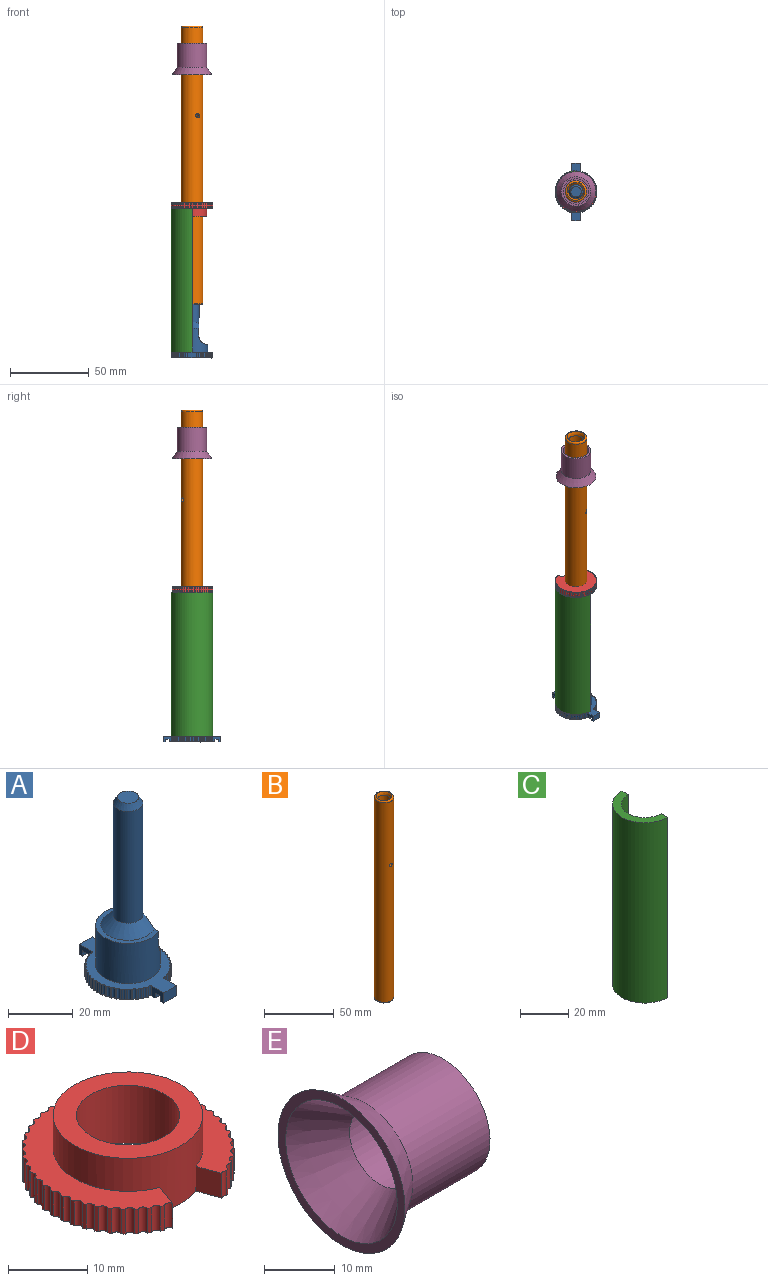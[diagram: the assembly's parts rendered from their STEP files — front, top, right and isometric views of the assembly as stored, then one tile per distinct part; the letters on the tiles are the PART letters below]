
ASSEMBLY  parts=5 mates=4
PART A: 110 faces, bbox 26.7x36.8x67.3 mm
  f0: plane 29.21x26.67mm, normal (0,0,-1), area 559.8mm2, adj f2,f3,f5,f6,f7,f8,f9,f10
  f1: plane 5.51x1.27mm, normal (0,0,-1), area 7mm2, adj f2,f99,f100,f106
  f2: plane 5.37x3.81mm, normal (1,0,0), area 15.6mm2, adj f0,f1,f49,f86,f100,f106,f107,f108
  f3: plane 5.37x3.81mm, normal (1,0,0), area 15.6mm2, adj f0,f4,f49,f54,f102,f103,f104,f105
  f4: plane 5.51x1.27mm, normal (0,0,-1), area 7mm2, adj f3,f101,f102,f104
  f5: cylinder r=13.33mm len=3.81mm, axis (0,0,-1), area 2mm2, adj f0,f49,f64,f96
  f6: cylinder r=13.33mm len=3.81mm, axis (0,0,-1), area 2mm2, adj f0,f49,f95,f96
  f7: cylinder r=13.33mm len=3.81mm, axis (0,0,-1), area 2mm2, adj f0,f49,f94,f95
  f8: cylinder r=13.33mm len=3.81mm, axis (0,0,-1), area 2mm2, adj f0,f49,f93,f94
  f9: cylinder r=13.33mm len=3.81mm, axis (0,0,-1), area 2mm2, adj f0,f49,f91,f92
  f10: cylinder r=13.33mm len=3.81mm, axis (0,0,-1), area 2mm2, adj f0,f49,f90,f91
  f11: cylinder r=13.33mm len=3.81mm, axis (0,0,-1), area 2mm2, adj f0,f49,f89,f90
  f12: cylinder r=13.33mm len=3.81mm, axis (0,0,-1), area 2mm2, adj f0,f49,f89,f93
  f13: cylinder r=13.33mm len=3.81mm, axis (0,0,-1), area 2mm2, adj f0,f49,f88,f92
  f14: cylinder r=13.33mm len=3.81mm, axis (0,0,-1), area 2mm2, adj f0,f49,f87,f88
  f15: cylinder r=13.33mm len=3.81mm, axis (0,0,-1), area 2mm2, adj f0,f49,f86,f87
  f16: cylinder r=13.33mm len=3.81mm, axis (0,0,-1), area 2mm2, adj f0,f49,f84,f85
  f17: cylinder r=13.33mm len=3.81mm, axis (0,0,-1), area 2mm2, adj f0,f49,f83,f84
  f18: cylinder r=13.33mm len=3.81mm, axis (0,0,-1), area 2mm2, adj f0,f49,f82,f83
  f19: cylinder r=13.33mm len=3.81mm, axis (0,0,-1), area 2mm2, adj f0,f49,f81,f82
  f20: cylinder r=13.33mm len=3.81mm, axis (0,0,-1), area 2mm2, adj f0,f49,f80,f81
  f21: cylinder r=13.33mm len=3.81mm, axis (0,0,-1), area 2mm2, adj f0,f49,f79,f80
  f22: cylinder r=13.33mm len=3.81mm, axis (0,0,-1), area 2mm2, adj f0,f49,f78,f79
  f23: cylinder r=13.33mm len=3.81mm, axis (0,0,-1), area 2mm2, adj f0,f49,f77,f78
  f24: cylinder r=13.33mm len=3.81mm, axis (0,0,-1), area 2mm2, adj f0,f49,f76,f77
  f25: cylinder r=13.33mm len=3.81mm, axis (0,0,-1), area 2mm2, adj f0,f49,f75,f76
  f26: cylinder r=13.33mm len=3.81mm, axis (0,0,-1), area 2mm2, adj f0,f49,f74,f75
  f27: cylinder r=13.33mm len=3.81mm, axis (0,0,-1), area 2mm2, adj f0,f49,f73,f74
  f28: cylinder r=13.33mm len=3.81mm, axis (0,0,-1), area 2mm2, adj f0,f49,f71,f72
  f29: cylinder r=13.33mm len=3.81mm, axis (0,0,-1), area 2mm2, adj f0,f49,f70,f71
  f30: cylinder r=13.33mm len=3.81mm, axis (0,0,-1), area 2mm2, adj f0,f49,f69,f70
  f31: cylinder r=13.33mm len=3.81mm, axis (0,0,-1), area 2mm2, adj f0,f49,f68,f69
  f32: cylinder r=13.33mm len=3.81mm, axis (0,0,-1), area 2mm2, adj f0,f49,f67,f68
  f33: cylinder r=13.33mm len=3.81mm, axis (0,0,-1), area 2mm2, adj f0,f49,f66,f67
  f34: cylinder r=13.33mm len=3.81mm, axis (0,0,-1), area 2mm2, adj f0,f49,f65,f66
  f35: cylinder r=13.33mm len=3.81mm, axis (0,0,-1), area 2mm2, adj f0,f49,f65,f73
  f36: cylinder r=13.33mm len=3.81mm, axis (0,0,-1), area 2mm2, adj f0,f49,f63,f64
  f37: cylinder r=13.33mm len=3.81mm, axis (0,0,-1), area 2mm2, adj f0,f49,f62,f63
  f38: cylinder r=13.33mm len=3.81mm, axis (0,0,-1), area 2mm2, adj f0,f49,f61,f62
  f39: cylinder r=13.33mm len=3.81mm, axis (0,0,-1), area 2mm2, adj f0,f49,f57,f61
  f40: cylinder r=13.33mm len=3.81mm, axis (0,0,-1), area 2mm2, adj f0,f49,f56,f60
  f41: cylinder r=13.33mm len=3.81mm, axis (0,0,-1), area 2mm2, adj f0,f49,f59,f60
  f42: cylinder r=13.33mm len=3.81mm, axis (0,0,-1), area 2mm2, adj f0,f49,f58,f59
  f43: cylinder r=13.33mm len=3.81mm, axis (0,0,-1), area 2mm2, adj f0,f49,f57,f58
  f44: cylinder r=13.33mm len=3.81mm, axis (0,0,-1), area 2mm2, adj f0,f49,f55,f56
  f45: cylinder r=13.33mm len=3.81mm, axis (0,0,-1), area 2mm2, adj f0,f49,f54,f55
  f46: cylinder r=10.02mm len=20.04mm, axis (0,0,-1), area 737.2mm2, adj f47,f49,f98
  f47: plane 20.04x14.18mm, normal (0,0,1), area 61.5mm2, adj f46,f97,f98
  f48: cylinder r=13.33mm len=3.81mm, axis (0,0,-1), area 2mm2, adj f0,f49,f53,f72
  f49: plane 36.83x26.67mm, normal (0,0,1), area 286.3mm2, adj f2,f3,f5,f6,f7,f8,f9,f10
  f50: cylinder r=4.57mm len=42.25mm, axis (0,0,-1), area 1205.6mm2, adj f52,f97,f98
  f51: plane 6.6x6.6mm, normal (0,0,1), area 34.3mm2, adj f52
  f52: cone r=3.3mm half-angle=30deg, axis (0,0,-1), area 62.8mm2, adj f50,f51
  f53: cylinder r=0.64mm len=3.81mm, axis (0,0,-1), area 5.5mm2, adj f0,f48,f49,f101
  f54: cylinder r=0.64mm len=3.81mm, axis (0,0,-1), area 5.5mm2, adj f0,f3,f45,f49
  f55: cylinder r=0.64mm len=3.81mm, axis (0,0,-1), area 5.5mm2, adj f0,f44,f45,f49
  f56: cylinder r=0.64mm len=3.81mm, axis (0,0,-1), area 5.5mm2, adj f0,f40,f44,f49
  f57: cylinder r=0.64mm len=3.81mm, axis (0,0,-1), area 5.5mm2, adj f0,f39,f43,f49
  f58: cylinder r=0.64mm len=3.81mm, axis (0,0,-1), area 5.5mm2, adj f0,f42,f43,f49
  f59: cylinder r=0.64mm len=3.81mm, axis (0,0,-1), area 5.5mm2, adj f0,f41,f42,f49
  f60: cylinder r=0.64mm len=3.81mm, axis (0,0,-1), area 5.5mm2, adj f0,f40,f41,f49
  f61: cylinder r=0.64mm len=3.81mm, axis (0,0,-1), area 5.5mm2, adj f0,f38,f39,f49
  f62: cylinder r=0.64mm len=3.81mm, axis (0,0,-1), area 5.5mm2, adj f0,f37,f38,f49
  f63: cylinder r=0.64mm len=3.81mm, axis (0,0,-1), area 5.5mm2, adj f0,f36,f37,f49
  f64: cylinder r=0.64mm len=3.81mm, axis (0,0,-1), area 5.5mm2, adj f0,f5,f36,f49
  f65: cylinder r=0.64mm len=3.81mm, axis (0,0,-1), area 5.5mm2, adj f0,f34,f35,f49
  f66: cylinder r=0.64mm len=3.81mm, axis (0,0,-1), area 5.5mm2, adj f0,f33,f34,f49
  f67: cylinder r=0.64mm len=3.81mm, axis (0,0,-1), area 5.5mm2, adj f0,f32,f33,f49
  f68: cylinder r=0.64mm len=3.81mm, axis (0,0,-1), area 5.5mm2, adj f0,f31,f32,f49
  f69: cylinder r=0.64mm len=3.81mm, axis (0,0,-1), area 5.5mm2, adj f0,f30,f31,f49
  f70: cylinder r=0.64mm len=3.81mm, axis (0,0,-1), area 5.5mm2, adj f0,f29,f30,f49
  f71: cylinder r=0.64mm len=3.81mm, axis (0,0,-1), area 5.5mm2, adj f0,f28,f29,f49
  f72: cylinder r=0.64mm len=3.81mm, axis (0,0,-1), area 5.5mm2, adj f0,f28,f48,f49
  f73: cylinder r=0.64mm len=3.81mm, axis (0,0,-1), area 5.5mm2, adj f0,f27,f35,f49
  f74: cylinder r=0.64mm len=3.81mm, axis (0,0,-1), area 5.5mm2, adj f0,f26,f27,f49
  f75: cylinder r=0.64mm len=3.81mm, axis (0,0,-1), area 5.5mm2, adj f0,f25,f26,f49
  f76: cylinder r=0.64mm len=3.81mm, axis (0,0,-1), area 5.5mm2, adj f0,f24,f25,f49
  f77: cylinder r=0.64mm len=3.81mm, axis (0,0,-1), area 5.5mm2, adj f0,f23,f24,f49
  f78: cylinder r=0.64mm len=3.81mm, axis (0,0,-1), area 5.5mm2, adj f0,f22,f23,f49
  f79: cylinder r=0.64mm len=3.81mm, axis (0,0,-1), area 5.5mm2, adj f0,f21,f22,f49
  f80: cylinder r=0.64mm len=3.81mm, axis (0,0,-1), area 5.5mm2, adj f0,f20,f21,f49
  f81: cylinder r=0.64mm len=3.81mm, axis (0,0,-1), area 5.5mm2, adj f0,f19,f20,f49
  f82: cylinder r=0.64mm len=3.81mm, axis (0,0,-1), area 5.5mm2, adj f0,f18,f19,f49
  f83: cylinder r=0.64mm len=3.81mm, axis (0,0,-1), area 5.5mm2, adj f0,f17,f18,f49
  f84: cylinder r=0.64mm len=3.81mm, axis (0,0,-1), area 5.5mm2, adj f0,f16,f17,f49
  f85: cylinder r=0.64mm len=3.81mm, axis (0,0,-1), area 5.5mm2, adj f0,f16,f49,f99
  f86: cylinder r=0.64mm len=3.81mm, axis (0,0,-1), area 5.5mm2, adj f0,f2,f15,f49
  f87: cylinder r=0.64mm len=3.81mm, axis (0,0,-1), area 5.5mm2, adj f0,f14,f15,f49
  f88: cylinder r=0.64mm len=3.81mm, axis (0,0,-1), area 5.5mm2, adj f0,f13,f14,f49
  f89: cylinder r=0.64mm len=3.81mm, axis (0,0,-1), area 5.5mm2, adj f0,f11,f12,f49
  f90: cylinder r=0.64mm len=3.81mm, axis (0,0,-1), area 5.5mm2, adj f0,f10,f11,f49
  f91: cylinder r=0.64mm len=3.81mm, axis (0,0,-1), area 5.5mm2, adj f0,f9,f10,f49
  f92: cylinder r=0.64mm len=3.81mm, axis (0,0,-1), area 5.5mm2, adj f0,f9,f13,f49
  f93: cylinder r=0.64mm len=3.81mm, axis (0,0,-1), area 5.5mm2, adj f0,f8,f12,f49
  f94: cylinder r=0.64mm len=3.81mm, axis (0,0,-1), area 5.5mm2, adj f0,f7,f8,f49
  f95: cylinder r=0.64mm len=3.81mm, axis (0,0,-1), area 5.5mm2, adj f0,f6,f7,f49
  f96: cylinder r=0.64mm len=3.81mm, axis (0,0,-1), area 5.5mm2, adj f0,f5,f6,f49
  f97: cone r=4.57mm half-angle=45deg, axis (0,0,-1), area 160.3mm2, adj f47,f50,f98
  f98: extruded ~18.29x18.11mm, area 262.4mm2, adj f46,f47,f50,f97
  f99: plane 5.37x3.81mm, normal (-1,0,0), area 15.6mm2, adj f0,f1,f49,f85,f100,f106,f107,f108
  f100: plane 5.51x3.81mm, normal (0,1,0), area 21mm2, adj f1,f2,f49,f99
  f101: plane 5.37x3.81mm, normal (-1,0,0), area 15.6mm2, adj f0,f4,f49,f53,f102,f103,f104,f105
  f102: plane 5.51x3.81mm, normal (0,-1,0), area 21mm2, adj f3,f4,f49,f101
  f103: plane 5.51x1.91mm, normal (0,-1,0), area 10.5mm2, adj f0,f3,f101,f105
  f104: plane 5.51x1.91mm, normal (0,1,0), area 10.5mm2, adj f3,f4,f101,f105
  f105: plane 5.51x2.54mm, normal (0,0,-1), area 14mm2, adj f3,f101,f103,f104
  f106: plane 5.51x1.91mm, normal (0,-1,0), area 10.5mm2, adj f1,f2,f99,f108
  f107: plane 5.51x1.91mm, normal (0,1,0), area 10.5mm2, adj f0,f2,f99,f108
  f108: plane 5.51x2.54mm, normal (0,0,-1), area 14mm2, adj f2,f99,f106,f107
  f109: torus R=8.33mm, axis (0,0,-1), area 391.7mm2
PART B: 8 faces, bbox 15x15x178.2 mm
  f0: cylinder r=6.95mm len=175.35mm, axis (0,0,-1), area 7639.8mm2, adj f2,f3,f6,f7
  f1: cylinder r=4.83mm len=172.38mm, axis (0,0,-1), area 5214.9mm2, adj f4,f5,f6,f7
  f2: torus R=5.72mm, axis (0,0,-1), area 78.7mm2, adj f0,f5
  f3: torus R=5.72mm, axis (0,0,-1), area 28.7mm2, adj f0,f4
  f4: cone r=4.83mm half-angle=45deg, axis (0,0,-1), area 100.2mm2, adj f1,f3
  f5: torus R=9.91mm, axis (0,0,1), area 98.5mm2, adj f1,f2
  f6: cylinder r=1.39mm len=2.78mm, axis (0,-1,0), area 18.8mm2, adj f0,f1
  f7: cylinder r=1.39mm len=2.78mm, axis (0,-1,0), area 18.8mm2, adj f0,f1
PART C: 6 faces, bbox 13.3x26.7x91.4 mm
  f0: cylinder r=9.65mm len=91.44mm, axis (0,0,-1), area 2772.7mm2, adj f2,f3,f4,f5
  f1: cylinder r=13.33mm len=91.44mm, axis (0,0,-1), area 3830.7mm2, adj f2,f3,f4,f5
  f2: plane 26.67x13.34mm, normal (0,0,1), area 133mm2, adj f0,f1,f4,f5
  f3: plane 26.67x13.34mm, normal (0,0,-1), area 133mm2, adj f0,f1,f4,f5
  f4: plane 91.44x3.68mm, normal (1,0,0), area 336.8mm2, adj f0,f1,f2,f3
  f5: plane 91.44x3.68mm, normal (1,0,0), area 336.8mm2, adj f0,f1,f2,f3
PART D: 96 faces, bbox 26.7x25.8x8.9 mm
  f0: plane 26.67x25.85mm, normal (0,0,-1), area 380.8mm2, adj f1,f2,f3,f4,f5,f6,f7,f8
  f1: cylinder r=0.64mm len=3.81mm, axis (0,0,-1), area 5.4mm2, adj f0,f23,f46,f95
  f2: cylinder r=13.33mm len=3.81mm, axis (0,0,-1), area 2mm2, adj f0,f46,f50,f93
  f3: cylinder r=13.33mm len=3.81mm, axis (0,0,-1), area 2mm2, adj f0,f46,f92,f93
  f4: cylinder r=13.33mm len=3.81mm, axis (0,0,-1), area 2mm2, adj f0,f46,f91,f92
  f5: cylinder r=13.33mm len=3.81mm, axis (0,0,-1), area 2mm2, adj f0,f46,f90,f91
  f6: cylinder r=13.33mm len=3.81mm, axis (0,0,-1), area 2mm2, adj f0,f46,f86,f90
  f7: cylinder r=13.33mm len=3.81mm, axis (0,0,-1), area 2mm2, adj f0,f46,f88,f89
  f8: cylinder r=13.33mm len=3.81mm, axis (0,0,-1), area 2mm2, adj f0,f46,f85,f89
  f9: cylinder r=13.33mm len=3.81mm, axis (0,0,-1), area 2mm2, adj f0,f46,f87,f88
  f10: cylinder r=13.33mm len=3.81mm, axis (0,0,-1), area 2mm2, adj f0,f46,f86,f87
  f11: cylinder r=13.33mm len=3.81mm, axis (0,0,-1), area 2mm2, adj f0,f46,f84,f85
  f12: cylinder r=13.33mm len=3.81mm, axis (0,0,-1), area 2mm2, adj f0,f46,f83,f84
  f13: cylinder r=13.33mm len=3.81mm, axis (0,0,-1), area 2mm2, adj f0,f46,f82,f83
  f14: cylinder r=13.33mm len=3.81mm, axis (0,0,-1), area 2mm2, adj f0,f46,f81,f82
  f15: cylinder r=13.33mm len=3.81mm, axis (0,0,-1), area 2mm2, adj f0,f46,f80,f81
  f16: cylinder r=13.33mm len=3.81mm, axis (0,0,-1), area 2mm2, adj f0,f46,f79,f80
  f17: cylinder r=13.33mm len=3.81mm, axis (0,0,-1), area 2mm2, adj f0,f46,f78,f79
  f18: cylinder r=13.33mm len=3.81mm, axis (0,0,-1), area 2mm2, adj f0,f46,f74,f78
  f19: cylinder r=13.33mm len=3.81mm, axis (0,0,-1), area 2mm2, adj f0,f46,f76,f77
  f20: cylinder r=13.33mm len=3.81mm, axis (0,0,-1), area 2mm2, adj f0,f46,f73,f77
  f21: cylinder r=13.33mm len=3.81mm, axis (0,0,-1), area 2mm2, adj f0,f46,f75,f76
  f22: cylinder r=13.33mm len=3.81mm, axis (0,0,-1), area 2mm2, adj f0,f46,f74,f75
  f23: cylinder r=13.33mm len=3.81mm, axis (0,0,-1), area 2mm2, adj f0,f1,f46,f73
  f24: cylinder r=13.33mm len=3.81mm, axis (0,0,-1), area 2mm2, adj f0,f46,f71,f72
  f25: cylinder r=13.33mm len=3.81mm, axis (0,0,-1), area 2mm2, adj f0,f46,f70,f71
  f26: cylinder r=13.33mm len=3.81mm, axis (0,0,-1), area 2mm2, adj f0,f46,f68,f70
  f27: cylinder r=13.33mm len=3.81mm, axis (0,0,-1), area 2mm2, adj f0,f46,f68,f69
  f28: cylinder r=13.33mm len=3.81mm, axis (0,0,-1), area 2mm2, adj f0,f46,f67,f69
  f29: cylinder r=13.33mm len=3.81mm, axis (0,0,-1), area 2mm2, adj f0,f46,f66,f67
  f30: cylinder r=13.33mm len=3.81mm, axis (0,0,-1), area 2mm2, adj f0,f46,f65,f66
  f31: cylinder r=13.33mm len=3.81mm, axis (0,0,-1), area 2mm2, adj f0,f46,f64,f65
  f32: cylinder r=13.33mm len=3.81mm, axis (0,0,-1), area 2mm2, adj f0,f46,f63,f64
  f33: cylinder r=13.33mm len=3.81mm, axis (0,0,-1), area 2mm2, adj f0,f46,f62,f63
  f34: cylinder r=13.33mm len=3.81mm, axis (0,0,-1), area 2mm2, adj f0,f46,f61,f62
  f35: cylinder r=13.33mm len=3.81mm, axis (0,0,-1), area 2mm2, adj f0,f46,f60,f61
  f36: cylinder r=13.33mm len=3.81mm, axis (0,0,-1), area 2mm2, adj f0,f46,f59,f60
  f37: cylinder r=13.33mm len=3.81mm, axis (0,0,-1), area 2mm2, adj f0,f46,f58,f59
  f38: cylinder r=13.33mm len=3.81mm, axis (0,0,-1), area 2mm2, adj f0,f46,f56,f58
  f39: cylinder r=13.33mm len=3.81mm, axis (0,0,-1), area 2mm2, adj f0,f46,f56,f57
  f40: cylinder r=13.33mm len=3.81mm, axis (0,0,-1), area 2mm2, adj f0,f46,f55,f57
  f41: cylinder r=13.33mm len=3.81mm, axis (0,0,-1), area 2mm2, adj f0,f46,f54,f55
  f42: cylinder r=13.33mm len=3.81mm, axis (0,0,-1), area 2mm2, adj f0,f46,f53,f54
  f43: cylinder r=13.33mm len=3.81mm, axis (0,0,-1), area 2mm2, adj f0,f46,f52,f53
  f44: cylinder r=13.33mm len=3.81mm, axis (0,0,-1), area 2mm2, adj f0,f46,f51,f52
  f45: cylinder r=13.33mm len=3.81mm, axis (0,0,-1), area 2mm2, adj f0,f46,f50,f51
  f46: plane 26.67x25.85mm, normal (0,0,1), area 234.6mm2, adj f1,f2,f3,f4,f5,f6,f7,f8
  f47: cylinder r=6.5mm len=13mm, axis (0,0,-1), area 363.1mm2, adj f0,f49
  f48: cylinder r=9.42mm len=18.85mm, axis (0,0,-1), area 325.8mm2, adj f0,f46,f49,f94,f95
  f49: plane 18.85x18.85mm, normal (0,0,1), area 146.2mm2, adj f47,f48
  f50: cylinder r=0.64mm len=3.81mm, axis (0,0,-1), area 5.5mm2, adj f0,f2,f45,f46
  f51: cylinder r=0.64mm len=3.81mm, axis (0,0,-1), area 5.5mm2, adj f0,f44,f45,f46
  f52: cylinder r=0.64mm len=3.81mm, axis (0,0,-1), area 5.5mm2, adj f0,f43,f44,f46
  f53: cylinder r=0.64mm len=3.81mm, axis (0,0,-1), area 5.5mm2, adj f0,f42,f43,f46
  f54: cylinder r=0.64mm len=3.81mm, axis (0,0,-1), area 5.5mm2, adj f0,f41,f42,f46
  f55: cylinder r=0.64mm len=3.81mm, axis (0,0,-1), area 5.5mm2, adj f0,f40,f41,f46
  f56: cylinder r=0.64mm len=3.81mm, axis (0,0,-1), area 5.5mm2, adj f0,f38,f39,f46
  f57: cylinder r=0.64mm len=3.81mm, axis (0,0,-1), area 5.5mm2, adj f0,f39,f40,f46
  f58: cylinder r=0.64mm len=3.81mm, axis (0,0,-1), area 5.5mm2, adj f0,f37,f38,f46
  f59: cylinder r=0.64mm len=3.81mm, axis (0,0,-1), area 5.5mm2, adj f0,f36,f37,f46
  f60: cylinder r=0.64mm len=3.81mm, axis (0,0,-1), area 5.5mm2, adj f0,f35,f36,f46
  f61: cylinder r=0.64mm len=3.81mm, axis (0,0,-1), area 5.5mm2, adj f0,f34,f35,f46
  f62: cylinder r=0.64mm len=3.81mm, axis (0,0,-1), area 5.5mm2, adj f0,f33,f34,f46
  f63: cylinder r=0.64mm len=3.81mm, axis (0,0,-1), area 5.5mm2, adj f0,f32,f33,f46
  f64: cylinder r=0.64mm len=3.81mm, axis (0,0,-1), area 5.5mm2, adj f0,f31,f32,f46
  f65: cylinder r=0.64mm len=3.81mm, axis (0,0,-1), area 5.5mm2, adj f0,f30,f31,f46
  f66: cylinder r=0.64mm len=3.81mm, axis (0,0,-1), area 5.5mm2, adj f0,f29,f30,f46
  f67: cylinder r=0.64mm len=3.81mm, axis (0,0,-1), area 5.5mm2, adj f0,f28,f29,f46
  f68: cylinder r=0.64mm len=3.81mm, axis (0,0,-1), area 5.5mm2, adj f0,f26,f27,f46
  f69: cylinder r=0.64mm len=3.81mm, axis (0,0,-1), area 5.5mm2, adj f0,f27,f28,f46
  f70: cylinder r=0.64mm len=3.81mm, axis (0,0,-1), area 5.5mm2, adj f0,f25,f26,f46
  f71: cylinder r=0.64mm len=3.81mm, axis (0,0,-1), area 5.5mm2, adj f0,f24,f25,f46
  f72: cylinder r=0.64mm len=3.81mm, axis (0,0,-1), area 3.4mm2, adj f0,f24,f46,f94
  f73: cylinder r=0.64mm len=3.81mm, axis (0,0,-1), area 5.5mm2, adj f0,f20,f23,f46
  f74: cylinder r=0.64mm len=3.81mm, axis (0,0,-1), area 5.5mm2, adj f0,f18,f22,f46
  f75: cylinder r=0.64mm len=3.81mm, axis (0,0,-1), area 5.5mm2, adj f0,f21,f22,f46
  f76: cylinder r=0.64mm len=3.81mm, axis (0,0,-1), area 5.5mm2, adj f0,f19,f21,f46
  f77: cylinder r=0.64mm len=3.81mm, axis (0,0,-1), area 5.5mm2, adj f0,f19,f20,f46
  f78: cylinder r=0.64mm len=3.81mm, axis (0,0,-1), area 5.5mm2, adj f0,f17,f18,f46
  f79: cylinder r=0.64mm len=3.81mm, axis (0,0,-1), area 5.5mm2, adj f0,f16,f17,f46
  f80: cylinder r=0.64mm len=3.81mm, axis (0,0,-1), area 5.5mm2, adj f0,f15,f16,f46
  f81: cylinder r=0.64mm len=3.81mm, axis (0,0,-1), area 5.5mm2, adj f0,f14,f15,f46
  f82: cylinder r=0.64mm len=3.81mm, axis (0,0,-1), area 5.5mm2, adj f0,f13,f14,f46
  f83: cylinder r=0.64mm len=3.81mm, axis (0,0,-1), area 5.5mm2, adj f0,f12,f13,f46
  f84: cylinder r=0.64mm len=3.81mm, axis (0,0,-1), area 5.5mm2, adj f0,f11,f12,f46
  f85: cylinder r=0.64mm len=3.81mm, axis (0,0,-1), area 5.5mm2, adj f0,f8,f11,f46
  f86: cylinder r=0.64mm len=3.81mm, axis (0,0,-1), area 5.5mm2, adj f0,f6,f10,f46
  f87: cylinder r=0.64mm len=3.81mm, axis (0,0,-1), area 5.5mm2, adj f0,f9,f10,f46
  f88: cylinder r=0.64mm len=3.81mm, axis (0,0,-1), area 5.5mm2, adj f0,f7,f9,f46
  f89: cylinder r=0.64mm len=3.81mm, axis (0,0,-1), area 5.5mm2, adj f0,f7,f8,f46
  f90: cylinder r=0.64mm len=3.81mm, axis (0,0,-1), area 5.5mm2, adj f0,f5,f6,f46
  f91: cylinder r=0.64mm len=3.81mm, axis (0,0,-1), area 5.5mm2, adj f0,f4,f5,f46
  f92: cylinder r=0.64mm len=3.81mm, axis (0,0,-1), area 5.5mm2, adj f0,f3,f4,f46
  f93: cylinder r=0.64mm len=3.81mm, axis (0,0,-1), area 5.5mm2, adj f0,f2,f3,f46
  f94: plane 3.81x3.34mm, normal (-0.94,-0.34,0), area 13.5mm2, adj f0,f46,f48,f72
  f95: plane 3.81x3.66mm, normal (0.94,-0.34,0), area 14.9mm2, adj f0,f1,f46,f48
PART E: 7 faces, bbox 20.3x25.4x25.4 mm
  f0: cone r=6mm half-angle=34.1deg, axis (-1,0,0), area 496.5mm2, adj f1,f6
  f1: plane 16.26x16.26mm, normal (1,0,0), area 94.5mm2, adj f0,f2
  f2: cylinder r=8.13mm len=16.26mm, axis (1,0,0), area 648.6mm2, adj f1,f3
  f3: plane 18.8x18.8mm, normal (1,0,0), area 69.9mm2, adj f2,f4
  f4: cylinder r=9.4mm len=18.8mm, axis (1,0,0), area 912.3mm2, adj f3,f5
  f5: cone r=12.7mm half-angle=34.1deg, axis (-1,0,0), area 408.5mm2, adj f4,f6
  f6: plane 25.4x25.4mm, normal (-1,0,0), area 115mm2, adj f0,f5
PLACE A t=(181.46,30.56,24.28)mm
PLACE B rot(axis=(0,0,1),31.1deg) t=(181.46,30.56,37.57)mm
PLACE C t=(181.46,30.56,28.09)mm
PLACE D rot(axis=(-1,0,0),180deg) t=(181.46,30.56,123.34)mm
PLACE E rot(axis=(-0.44,-0.78,-0.44),104deg) t=(181.46,30.56,212.16)mm
MATE cylindrical E.f0 <-> B.f0  axis (0,0,1) through (181.46,30.56,224.86)mm
MATE fastened D.f48 <-> C.f0  axis (0,0,-1) through (181.46,30.56,119.53)mm
MATE cylindrical B.f0 <-> C.f0  axis (0,0,-1) through (181.46,30.56,146.79)mm
MATE revolute A.f46 <-> C.f0  axis (0,0,1) through (181.46,30.56,28.09)mm
